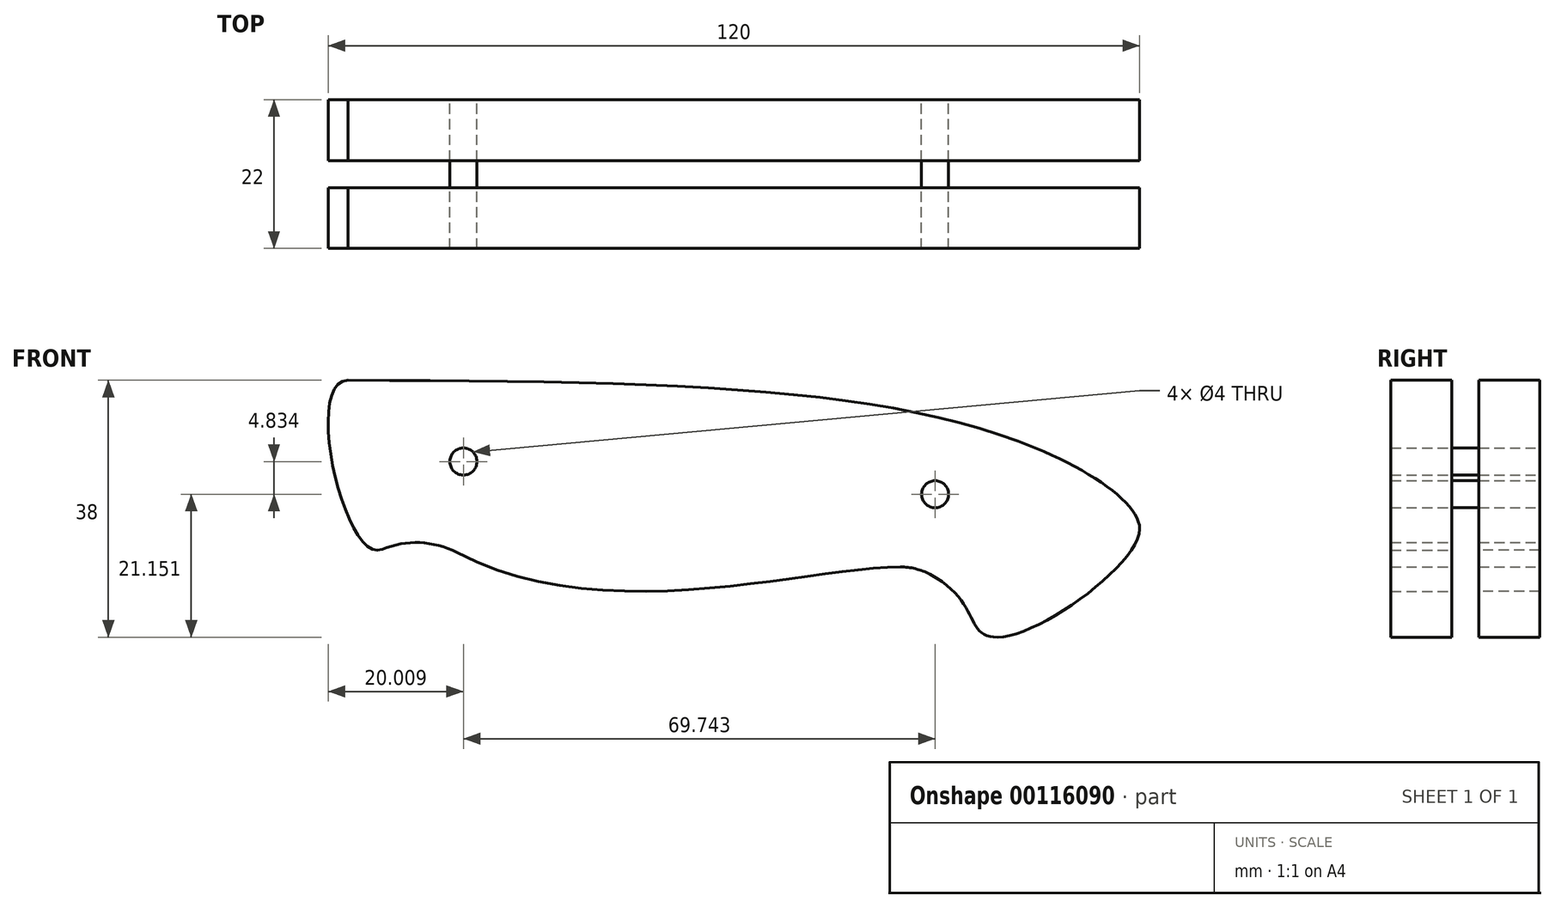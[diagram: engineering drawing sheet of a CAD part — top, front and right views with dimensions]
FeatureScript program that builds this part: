
annotation { "Feature Type Name" : "Feature", "Feature Type Description" : "" }
export const myFeature = defineFeature(function(context is Context, id is Id, definition is map)
    precondition{}
    {
        {
            var Q0;
            Q0=qCreatedBy(makeId("Front.planeOp"),FACE);
            var sketch = newSketch(context, id + "F0", { "sketchPlane" : qUnion([Q0])});
            skLineSegment(sketch, "E0.bottom", {"start": v(0, 0) * mm, "end": v(230, 0) * mm});
            skLineSegment(sketch, "E0.top", {"start": v(0, -38) * mm, "end": v(230, -38) * mm});
            skLineSegment(sketch, "E0.left", {"start": v(0, 0) * mm, "end": v(0, -38) * mm});
            skLineSegment(sketch, "E0.right", {"start": v(230, 0) * mm, "end": v(230, -38) * mm});
            skSolve(sketch);
        }
        {
            var Q0;
            Q0=makeQuery(id+"F0.imprint","IMPRINT",FACE,{"disambiguationData":[TD([[makeQuery(id+"F0.imprint","IMPRINT",EDGE,{"derivedFrom":sQuery(id+"F0.wireOp",EDGE,"E0.bottom")}),-1.0]])]});
            var sketch = newSketch(context, id + "F1", { "sketchPlane" : qUnion([Q0])});
            skLineSegment(sketch, "E1", {"start": v(0, 0) * mm, "end": v(0, -10) * mm, "construction": true});
            skLineSegment(sketch, "E2", {"start": v(110, 0) * mm, "end": v(230, 0) * mm, "construction": true});
            skLineSegment(sketch, "E3", {"start": v(110, 0) * mm, "end": v(110, -38) * mm, "construction": true});
            skFitSpline(sketch, "E4", {"points": [v(0, -10) * mm, v(110, -38) * mm], "startDerivative": vector(51, -84) * mm, "endDerivative": vector(120, 0) * mm});
            skFitSpline(sketch, "E5", {"points": [v(0, -10) * mm, v(110, 0) * mm], "startDerivative": vector(150, 30) * mm, "endDerivative": vector(210, 0) * mm});
            skLineSegment(sketch, "E6", {"start": v(110, -38) * mm, "end": v(70, -38) * mm, "construction": true});
            skLineSegment(sketch, "E7", {"start": v(110, 0) * mm, "end": v(40, 0) * mm, "construction": true});
            skLineSegment(sketch, "E8", {"start": v(110, 0) * mm, "end": v(0, 0) * mm, "construction": true});
            skLineSegment(sketch, "E9", {"start": v(110, -38) * mm, "end": v(123, -38) * mm, "construction": true});
            skLineSegment(sketch, "E10", {"start": v(123, -38) * mm, "end": v(123, -37) * mm, "construction": true});
            skArc(sketch, "E11", {"start": v(129, -25.47) * mm, "mid": v(116.25, -25.89) * mm, "end": v(110, -37) * mm});
            skFitSpline(sketch, "E12", {"points": [v(110, 0) * mm, v(212, -9) * mm, v(230, -22) * mm], "startDerivative": vector(219.85, 0) * mm, "endDerivative": vector(0, -37.77) * mm});
            skLineSegment(sketch, "E13", {"start": v(230, 0) * mm, "end": v(230, -22) * mm, "construction": true});
            skLineSegment(sketch, "E14", {"start": v(110, 0) * mm, "end": v(160, 0) * mm, "construction": true});
            skLineSegment(sketch, "E15", {"start": v(230, -22) * mm, "end": v(230, -18) * mm, "construction": true});
            skLineSegment(sketch, "E16", {"start": v(230, -38) * mm, "end": v(209, -38) * mm, "construction": true});
            skFitSpline(sketch, "E17", {"points": [v(230, -22) * mm, v(209, -38) * mm], "startDerivative": vector(0, -15.6) * mm, "endDerivative": vector(-18, 0) * mm});
            skLineSegment(sketch, "E18", {"start": v(230, -22) * mm, "end": v(230, -27.2) * mm, "construction": true});
            skLineSegment(sketch, "E19", {"start": v(209, -38) * mm, "end": v(215, -38) * mm, "construction": true});
            skLineSegment(sketch, "E20", {"start": v(129, -25.47) * mm, "end": v(151.18, -37) * mm, "construction": true});
            skArc(sketch, "E21", {"start": v(199, -28.7) * mm, "mid": v(196.87, -27.88) * mm, "end": v(194.6, -27.6) * mm});
            skLineSegment(sketch, "E22", {"start": v(194.6, -27.6) * mm, "end": v(180.6, -27.6) * mm, "construction": true});
            skFitSpline(sketch, "E23", {"points": [v(129, -25.47) * mm, v(194.6, -27.6) * mm], "startDerivative": vector(66.53, -34.62) * mm, "endDerivative": vector(42, 0) * mm});
            skLineSegment(sketch, "E24", {"start": v(204, -38) * mm, "end": v(209, -38) * mm, "construction": true});
            skLineSegment(sketch, "E25", {"start": v(194.6, -37) * mm, "end": v(204, -37) * mm, "construction": true});
            skLineSegment(sketch, "E26", {"start": v(199, -28.7) * mm, "end": v(206.6, -32.72) * mm, "construction": true});
            skFitSpline(sketch, "E27", {"points": [v(199, -28.7) * mm, v(209, -38) * mm], "startDerivative": vector(22.8, -12.08) * mm, "endDerivative": vector(15, 0) * mm});
            skLineSegment(sketch, "E28", {"start": v(209, -38) * mm, "end": v(204, -38) * mm, "construction": true});
            skLineSegment(sketch, "E29", {"start": v(0, -38) * mm, "end": v(17, -38) * mm, "construction": true});
            skLineSegment(sketch, "E30", {"start": v(0, 0) * mm, "end": v(50, 0) * mm});
            skLineSegment(sketch, "E31", {"start": v(110, -25.47) * mm, "end": v(129, -25.47) * mm, "construction": true});
            skLineSegment(sketch, "E32", {"start": v(194.6, -27.6) * mm, "end": v(230, -27.6) * mm, "construction": true});
            skLineSegment(sketch, "E33", {"start": v(204, -38) * mm, "end": v(204, -37) * mm, "construction": true});
            skLineSegment(sketch, "E34", {"start": v(110, -38) * mm, "end": v(106, -38) * mm, "construction": true});
            skLineSegment(sketch, "E35", {"start": v(106, -38) * mm, "end": v(106, -10) * mm, "construction": true});
            skLineSegment(sketch, "E36", {"start": v(106, -10) * mm, "end": v(96, -10) * mm, "construction": true});
            skLineSegment(sketch, "E37", {"start": v(96, -10) * mm, "end": v(96, -20) * mm, "construction": true});
            skArc(sketch, "E38", {"start": v(106, -20) * mm, "mid": v(103.07, -12.93) * mm, "end": v(96, -10) * mm});
            skPoint(sketch, "E39", {"position": v(106, -20) * mm});
            skLineSegment(sketch, "E40", {"start": v(106, -20) * mm, "end": v(106, -38) * mm});
            skLineSegment(sketch, "E41", {"start": v(110, 0) * mm, "end": v(113, 0) * mm, "construction": true});
            skLineSegment(sketch, "E42", {"start": v(118, -25) * mm, "end": v(112.46, -27.3) * mm, "construction": true});
            skLineSegment(sketch, "E43", {"start": v(118, -25) * mm, "end": v(110, -25) * mm, "construction": true});
            skFitSpline(sketch, "E44", {"points": [v(113, 0) * mm, v(118, -25) * mm], "startDerivative": vector(-20.6, 0) * mm, "endDerivative": vector(16.62, 6.92) * mm});
            skLineSegment(sketch, "E45", {"start": v(96, -10) * mm, "end": v(96, 0) * mm});
            skLineSegment(sketch, "E46", {"start": v(110, -37) * mm, "end": v(110, -38) * mm});
            skLineSegment(sketch, "E47", {"start": v(110, -9) * mm, "end": v(212, -9) * mm, "construction": true});
            skLineSegment(sketch, "E48", {"start": v(212, 0) * mm, "end": v(212, -9) * mm});
            skLineSegment(sketch, "E49", {"start": v(199, -28.7) * mm, "end": v(230, -28.7) * mm, "construction": true});
            skFitSpline(sketch, "E50", {"points": [v(208, -7.62) * mm, v(214, -36.61) * mm], "startDerivative": vector(40.02, -12.74) * mm, "endDerivative": vector(-21.9, -9.84) * mm, "construction": true});
            skLineSegment(sketch, "E51", {"start": v(208, -7.62) * mm, "end": v(221.34, -11.87) * mm, "construction": true});
            skLineSegment(sketch, "E52", {"start": v(214, -36.61) * mm, "end": v(221.3, -33.33) * mm, "construction": true});
            skLineSegment(sketch, "E53", {"start": v(208, -7.62) * mm, "end": v(230, -7.62) * mm, "construction": true});
            skLineSegment(sketch, "E54", {"start": v(214, -36.61) * mm, "end": v(230, -36.61) * mm, "construction": true});
            skSolve(sketch);
        }
        {
            var Q0;
            Q0=makeQuery(id+"F0.imprint","IMPRINT",FACE,{"disambiguationData":[TD([[makeQuery(id+"F0.imprint","IMPRINT",EDGE,{"derivedFrom":sQuery(id+"F0.wireOp",EDGE,"E0.bottom")}),-1.0]])]});
            var sketch = newSketch(context, id + "F2", { "sketchPlane" : qUnion([Q0])});
            skLineSegment(sketch, "E55", {"start": v(123, -24) * mm, "end": v(123, 0) * mm, "construction": true});
            skLineSegment(sketch, "E56", {"start": v(198.06, -28.26) * mm, "end": v(206.44, -7.14) * mm, "construction": true});
            skFitSpline(sketch, "E57", {"points": [v(123, -12) * mm, v(202.25, -17.7) * mm], "startDerivative": vector(111, 0) * mm, "endDerivative": vector(34.3, -13.6) * mm, "construction": true});
            skLineSegment(sketch, "E58", {"start": v(202.25, -17.7) * mm, "end": v(190.82, -13.17) * mm, "construction": true});
            skCircle(sketch, "E59", {"center": v(130, -12.01) * mm, "radius": 2 * mm});
            skCircle(sketch, "E60", {"center": v(199.75, -16.85) * mm, "radius": 2 * mm});
            skSolve(sketch);
        }
        {
            var Q0;
            {var subQ8=sQuery(id+"F1.wireOp",EDGE,"E5");Q0=makeQuery(id+"F1.imprint","IMPRINT",FACE,{"disambiguationData":[TD([[makeQuery(id+"F1.imprint","IMPRINT",EDGE,{"derivedFrom":subQ8}),-1.0]])]});}
            extrude(context, id + "F3", {"entities" : qUnion([Q0]), "endBound" : BoundingType.SYMMETRIC, "depth" : 4 * mm});
        }
        {
            var Q0;
            Q0=makeQuery(id+"F3.opExtrude","CAP_EDGE",EDGE,{"disambiguationData":[OSD([sQuery(id+"F1.wireOp",EDGE,"E4")])],"isStart":false});
            var Q1;
            Q1=makeQuery(id+"F3.opExtrude","CAP_EDGE",EDGE,{"disambiguationData":[OSD([sQuery(id+"F1.wireOp",EDGE,"E4")])],"isStart":true});
            chamfer(context, id + "F4", {"entities" : qUnion([Q0, Q1]), "chamferType" : ChamferType.TWO_OFFSETS, "width1" : 28 * mm, "oppositeDirection" : false, "width2" : 2 * mm, "tangentPropagation" : true});
        }
        {
            var Q0;
            {var subQ15=sQuery(id+"F1.wireOp",EDGE,"E38");Q0=makeQuery(id+"F1.imprint","IMPRINT",FACE,{"disambiguationData":[TD([[makeQuery(id+"F1.imprint","IMPRINT",EDGE,{"derivedFrom":subQ15}),-1.0]])]});}
            var Q1;
            Q1=makeQuery(id+"F1.imprint","IMPRINT",FACE,{"disambiguationData":[TD([[makeQuery(id+"F1.imprint","IMPRINT",EDGE,{"derivedFrom":sQuery(id+"F1.wireOp",EDGE,"E21")}),-1.0]])]});
            extrude(context, id + "F5", {"entities" : qUnion([Q0, Q1]), "operationType" : NewBodyOperationType.ADD, "endBound" : BoundingType.SYMMETRIC, "depth" : 4 * mm});
        }
        {
            var Q0;
            Q0=makeQuery(id+"F1.imprint","IMPRINT",FACE,{"disambiguationData":[TD([[makeQuery(id+"F1.imprint","IMPRINT",EDGE,{"derivedFrom":sQuery(id+"F1.wireOp",EDGE,"E21")}),-1.0]])]});
            extrude(context, id + "F6", {"entities" : qUnion([Q0]), "endBound" : BoundingType.SYMMETRIC, "depth" : 22 * mm});
        }
        {
            var Q0;
            Q0 = qSketchRegion(id + "F0", true);
            extrude(context, id + "F7", {"entities" : qUnion([Q0]), "operationType" : NewBodyOperationType.REMOVE, "endBound" : BoundingType.SYMMETRIC, "depth" : 4 * mm});
        }
        {
            var Q0;
            Q0=makeQuery(id+"F2.imprint","IMPRINT",FACE,{"disambiguationData":[TD([[makeQuery(id+"F2.imprint","IMPRINT",EDGE,{"derivedFrom":sQuery(id+"F2.wireOp",EDGE,"E59")}),1.0]])]});
            var Q1;
            Q1=makeQuery(id+"F2.imprint","IMPRINT",FACE,{"disambiguationData":[TD([[makeQuery(id+"F2.imprint","IMPRINT",EDGE,{"derivedFrom":sQuery(id+"F2.wireOp",EDGE,"E60")}),1.0]])]});
            extrude(context, id + "F8", {"entities" : qUnion([Q0, Q1]), "endBound" : BoundingType.SYMMETRIC, "depth" : 22 * mm});
        }
        {
            var Q0;
            Q0=makeQuery(id+"F8.opExtrude","SWEPT_BODY",BODY,{"disambiguationData":[OSD([sQuery(id+"F2.wireOp",EDGE,"E59")])]});
            var Q1;
            Q1=makeQuery(id+"F8.opExtrude","SWEPT_BODY",BODY,{"disambiguationData":[OSD([sQuery(id+"F2.wireOp",EDGE,"E60")])]});
            var Q2;
            Q2=makeQuery(id+"F3.opExtrude","SWEPT_BODY",BODY,{"disambiguationData":[OSD([sQuery(id+"F1.wireOp",EDGE,"E4"),sQuery(id+"F1.wireOp",EDGE,"E5"),sQuery(id+"F1.wireOp",EDGE,"E38"),sQuery(id+"F1.wireOp",EDGE,"E40"),sQuery(id+"F1.wireOp",EDGE,"E45")])]});
            var Q3;
            Q3=makeQuery(id+"F7.boolean.opBoolean","SPLIT",BODY,{"disambiguationData":[OD(0.0)],"derivedFrom":makeQuery(id+"F6.opExtrude","SWEPT_BODY",BODY,{"disambiguationData":[OSD([sQuery(id+"F1.wireOp",EDGE,"E11"),sQuery(id+"F1.wireOp",EDGE,"E12"),sQuery(id+"F1.wireOp",EDGE,"E17"),sQuery(id+"F1.wireOp",EDGE,"E21"),sQuery(id+"F1.wireOp",EDGE,"E23"),sQuery(id+"F1.wireOp",EDGE,"E27"),sQuery(id+"F1.wireOp",EDGE,"E44")])]})});
            var Q4;
            Q4=makeQuery(id+"F7.boolean.opBoolean","SPLIT",BODY,{"disambiguationData":[OD(1.0)],"derivedFrom":makeQuery(id+"F6.opExtrude","SWEPT_BODY",BODY,{"disambiguationData":[OSD([sQuery(id+"F1.wireOp",EDGE,"E11"),sQuery(id+"F1.wireOp",EDGE,"E12"),sQuery(id+"F1.wireOp",EDGE,"E17"),sQuery(id+"F1.wireOp",EDGE,"E21"),sQuery(id+"F1.wireOp",EDGE,"E23"),sQuery(id+"F1.wireOp",EDGE,"E27"),sQuery(id+"F1.wireOp",EDGE,"E44")])]})});
            booleanBodies(context, id + "F9", {"operationType" : BooleanOperationType.SUBTRACTION, "tools" : qUnion([Q0, Q1]), "targets" : qUnion([Q2, Q3, Q4]), "keepTools" : true});
        }
    });
